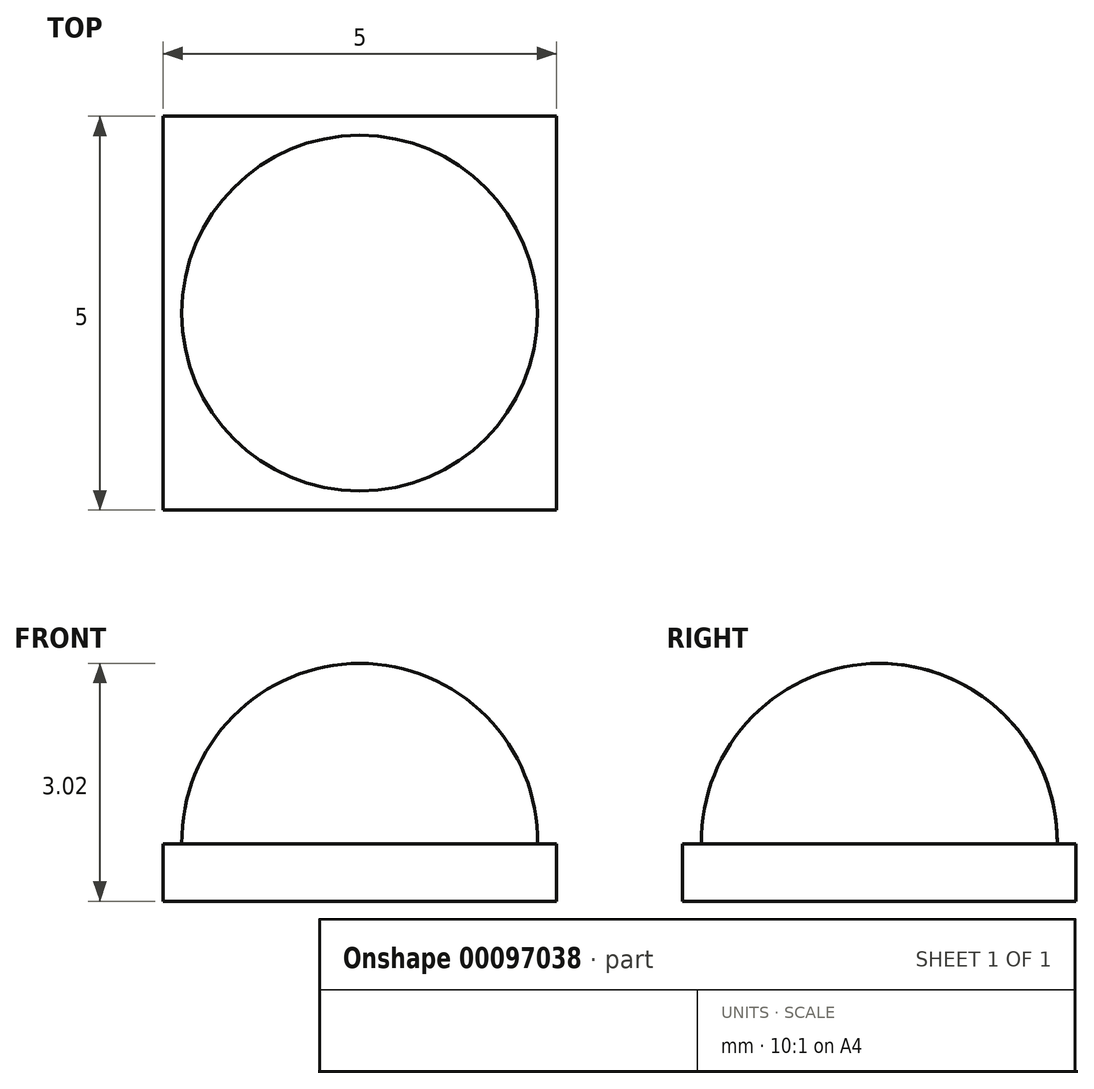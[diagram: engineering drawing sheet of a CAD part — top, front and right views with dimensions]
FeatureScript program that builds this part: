
annotation { "Feature Type Name" : "Feature", "Feature Type Description" : "" }
export const myFeature = defineFeature(function(context is Context, id is Id, definition is map)
    precondition{}
    {
        {
            var Q0;
            Q0=qCreatedBy(makeId("Top.planeOp"),FACE);
            var sketch = newSketch(context, id + "F0", { "sketchPlane" : qUnion([Q0])});
            skLineSegment(sketch, "E0.bottom", {"start": v(2.5, 2.5) * mm, "end": v(-2.5, 2.5) * mm});
            skLineSegment(sketch, "E0.top", {"start": v(2.5, -2.5) * mm, "end": v(-2.5, -2.5) * mm});
            skLineSegment(sketch, "E0.left", {"start": v(2.5, 2.5) * mm, "end": v(2.5, -2.5) * mm});
            skLineSegment(sketch, "E0.right", {"start": v(-2.5, 2.5) * mm, "end": v(-2.5, -2.5) * mm});
            skPoint(sketch, "E0.middle", {"position": v(0, 0) * mm});
            skSolve(sketch);
        }
        {
            var Q0;
            Q0 = qSketchRegion(id + "F0", true);
            extrude(context, id + "F1", {"entities" : qUnion([Q0]), "depth" : .73 * mm});
        }
        {
            var Q0;
            Q0=qCreatedBy(makeId("Right.planeOp"),FACE);
            var sketch = newSketch(context, id + "F2", { "sketchPlane" : qUnion([Q0])});
            skLineSegment(sketch, "E1", {"start": v(0, 0.73) * mm, "end": v(0, 3.02) * mm});
            skArc(sketch, "E2", {"start": v(2.26, 0.73) * mm, "mid": v(1.6, 2.35) * mm, "end": v(0, 3.02) * mm});
            skLineSegment(sketch, "E3", {"start": v(0, 0.73) * mm, "end": v(2.26, 0.73) * mm});
            skLineSegment(sketch, "E4", {"start": v(0, 3.02) * mm, "end": v(-1.18, 3.02) * mm, "construction": true});
            skSolve(sketch);
        }
        {
            var Q0;
            Q0=makeQuery(id+"F2.imprint","IMPRINT",FACE,{"disambiguationData":[TD([[makeQuery(id+"F2.imprint","IMPRINT",EDGE,{"derivedFrom":sQuery(id+"F2.wireOp",EDGE,"E1")}),-1.0]])]});
            var Q1;
            Q1=sQuery(id+"F2.wireOp",EDGE,"E1");
            revolve(context, id + "F3", {"operationType" : NewBodyOperationType.ADD, "entities" : qUnion([Q0]), "axis" : qUnion([Q1]), "revolveType" : RevolveType.FULL});
        }
    });
